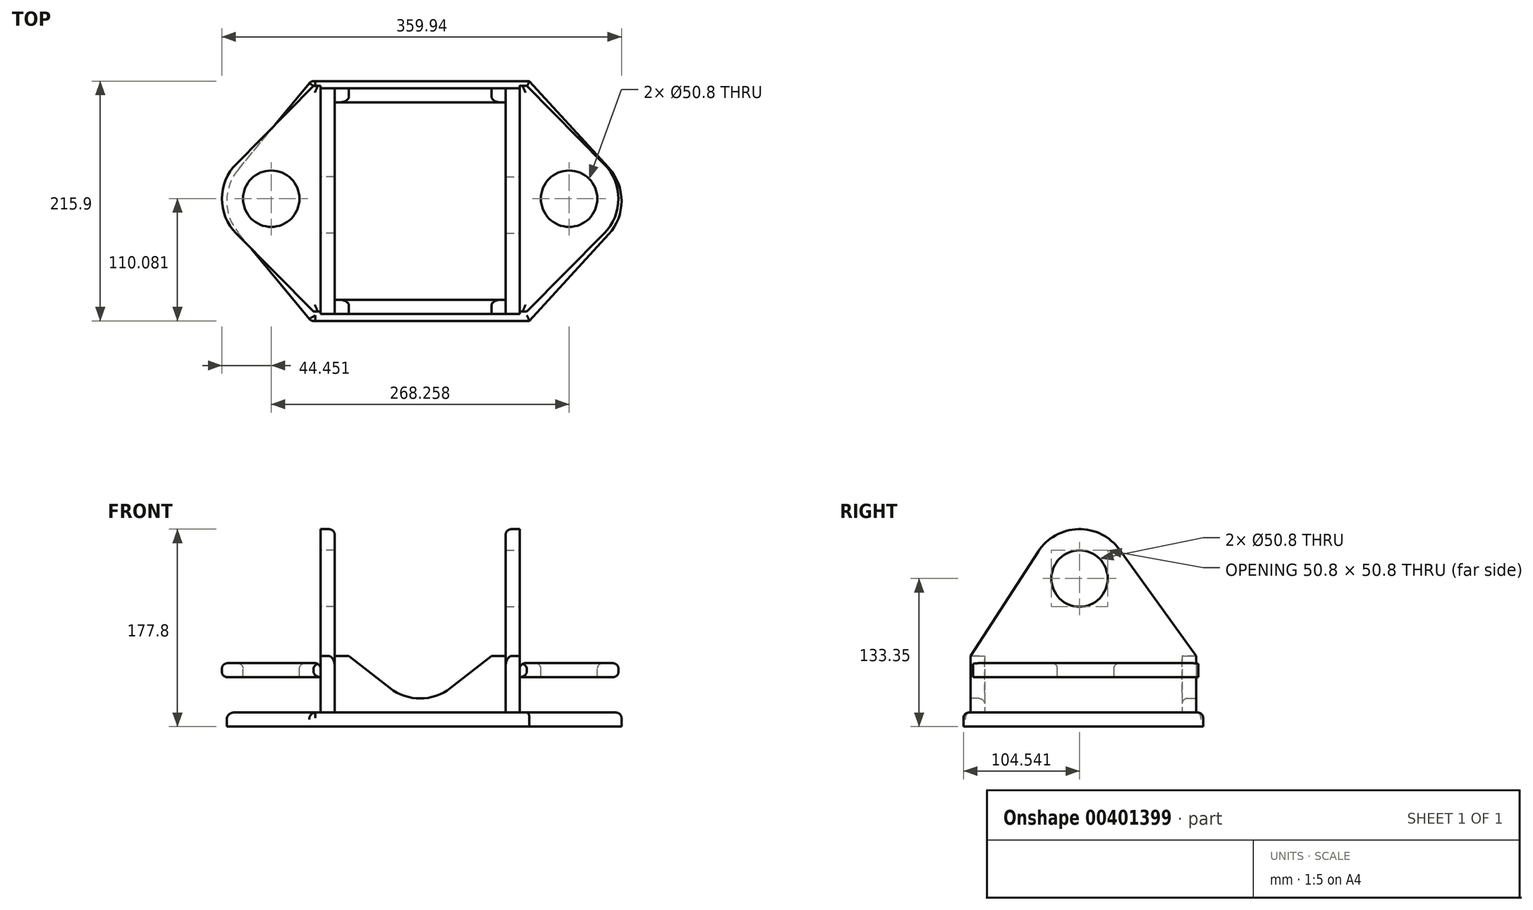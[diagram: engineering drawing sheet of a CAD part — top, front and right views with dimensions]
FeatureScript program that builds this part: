
annotation { "Feature Type Name" : "Feature", "Feature Type Description" : "" }
export const myFeature = defineFeature(function(context is Context, id is Id, definition is map)
    precondition{}
    {
        {
            var Q0;
            Q0=qCreatedBy(makeId("Top.planeOp"),FACE);
            var sketch = newSketch(context, id + "F0", { "sketchPlane" : qUnion([Q0])});
            skLineSegment(sketch, "E0.bottom", {"start": v(-98.42, 107.95) * mm, "end": v(98.43, 107.95) * mm});
            skLineSegment(sketch, "E0.top", {"start": v(-98.43, -107.95) * mm, "end": v(98.42, -107.95) * mm});
            skPoint(sketch, "E0.middle", {"position": v(0, 0) * mm});
            skArc(sketch, "E1", {"start": v(-164.1, 28.27) * mm, "mid": v(-174.24, 0) * mm, "end": v(-164.1, -28.27) * mm});
            skArc(sketch, "E2", {"start": v(169.7, -30) * mm, "mid": v(181.36, 0) * mm, "end": v(169.7, 30) * mm});
            skLineSegment(sketch, "E3", {"start": v(-98.43, -107.95) * mm, "end": v(-164.1, -28.27) * mm});
            skLineSegment(sketch, "E4", {"start": v(98.43, 107.95) * mm, "end": v(169.7, 30) * mm});
            skLineSegment(sketch, "E5", {"start": v(98.42, -107.95) * mm, "end": v(169.7, -30) * mm});
            skLineSegment(sketch, "E6", {"start": v(-98.43, 107.95) * mm, "end": v(-164.1, 28.27) * mm});
            skLineSegment(sketch, "E7", {"start": v(-174.24, 0) * mm, "end": v(181.36, 0) * mm, "construction": true});
            skSolve(sketch);
        }
        {
            var Q0;
            Q0 = qSketchRegion(id + "F0", true);
            extrude(context, id + "F1", {"entities" : qUnion([Q0]), "oppositeDirection" : true, "depth" : 12.7 * mm});
        }
        {
            var Q0;
            Q0=makeQuery(id+"F1.opExtrude","CAP_EDGE",EDGE,{"disambiguationData":[OSD([sQuery(id+"F0.wireOp",EDGE,"E6")])],"isStart":true});
            fillet(context, id + "F2", {"entities" : qUnion([Q0]), "radius" : 6.35 * mm, "tangentPropagation" : true, "allowEdgeOverflow" : false});
        }
        {
            var Q0;
            Q0=makeQuery(id+"F1.opExtrude","CAP_EDGE",EDGE,{"disambiguationData":[OSD([sQuery(id+"F0.wireOp",EDGE,"E0.bottom")])],"isStart":true});
            var Q1;
            Q1=makeQuery(id+"F1.opExtrude","CAP_EDGE",EDGE,{"disambiguationData":[OSD([sQuery(id+"F0.wireOp",EDGE,"E0.top")])],"isStart":true});
            var Q2;
            Q2=makeQuery(id+"F1.opExtrude","CAP_EDGE",EDGE,{"disambiguationData":[OSD([sQuery(id+"F0.wireOp",EDGE,"E5")])],"isStart":true});
            fillet(context, id + "F3", {"entities" : qUnion([Q0, Q1, Q2]), "radius" : 5.08 * mm, "tangentPropagation" : true, "allowEdgeOverflow" : false});
        }
        {
            var Q0;
            Q0=makeQuery(id+"F1.opExtrude","CAP_FACE",FACE,{"disambiguationData":[OSD([sQuery(id+"F0.wireOp",EDGE,"E0.bottom"),sQuery(id+"F0.wireOp",EDGE,"E0.top"),sQuery(id+"F0.wireOp",EDGE,"E1"),sQuery(id+"F0.wireOp",EDGE,"E2"),sQuery(id+"F0.wireOp",EDGE,"E3"),sQuery(id+"F0.wireOp",EDGE,"E4"),sQuery(id+"F0.wireOp",EDGE,"E5"),sQuery(id+"F0.wireOp",EDGE,"E6")])],"isStart":true});
            var sketch = newSketch(context, id + "F4", { "sketchPlane" : qUnion([Q0])});
            skLineSegment(sketch, "E8.bottom", {"start": v(-89.68, 101.6) * mm, "end": v(-76.98, 101.6) * mm});
            skLineSegment(sketch, "E8.top", {"start": v(-89.68, -101.6) * mm, "end": v(-76.98, -101.6) * mm});
            skLineSegment(sketch, "E8.left", {"start": v(-89.68, 101.6) * mm, "end": v(-89.68, -101.6) * mm});
            skLineSegment(sketch, "E8.right", {"start": v(-76.98, 101.6) * mm, "end": v(-76.98, -101.6) * mm});
            skSolve(sketch);
        }
        {
            var Q0;
            Q0 = qSketchRegion(id + "F4", true);
            extrude(context, id + "F5", {"entities" : qUnion([Q0]), "depth" : 165.1 * mm});
        }
        {
            var Q0;
            Q0=makeQuery(id+"F5.opExtrude","SWEPT_FACE",FACE,{"disambiguationData":[OSD([sQuery(id+"F4.wireOp",EDGE,"E8.left")])]});
            var sketch = newSketch(context, id + "F6", { "sketchPlane" : qUnion([Q0])});
            skLineSegment(sketch, "E9", {"start": v(-101.6, 50.8) * mm, "end": v(101.6, 50.8) * mm, "construction": true});
            skCircle(sketch, "E10", {"center": v(3.4, 120.65) * mm, "radius": 25.4 * mm});
            skArc(sketch, "E11", {"start": v(40.72, 144.81) * mm, "mid": v(4.5, 165.09) * mm, "end": v(-32.67, 146.6) * mm});
            skLineSegment(sketch, "E12", {"start": v(-101.6, 50.8) * mm, "end": v(-32.67, 146.6) * mm});
            skLineSegment(sketch, "E13", {"start": v(101.6, 50.8) * mm, "end": v(40.72, 144.81) * mm});
            skSolve(sketch);
        }
        {
            var Q0;
            Q0 = qSketchRegion(id + "F6", true);
            var Q1;
            {var subQ0=sQuery(id+"F6.wireOp",EDGE,"E12");Q1=makeQuery(id+"F6.imprint","IMPRINT",FACE,{"disambiguationData":[TD([[makeQuery(id+"F6.imprint","IMPRINT",EDGE,{"derivedFrom":subQ0}),1.0]])]});}
            var Q2;
            {var subQ0=sQuery(id+"F6.wireOp",EDGE,"E13");Q2=makeQuery(id+"F6.imprint","IMPRINT",FACE,{"disambiguationData":[TD([[makeQuery(id+"F6.imprint","IMPRINT",EDGE,{"derivedFrom":subQ0}),-1.0]])]});}
            extrude(context, id + "F7", {"entities" : qUnion([Q0, Q1, Q2]), "operationType" : NewBodyOperationType.REMOVE, "oppositeDirection" : true, "depth" : 25.4 * mm});
        }
        {
            var Q0;
            Q0=makeQuery(id+"F5.opExtrude","SWEPT_BODY",BODY,{"disambiguationData":[OSD([sQuery(id+"F4.wireOp",EDGE,"E8.bottom"),sQuery(id+"F4.wireOp",EDGE,"E8.top"),sQuery(id+"F4.wireOp",EDGE,"E8.left"),sQuery(id+"F4.wireOp",EDGE,"E8.right")])]});
            var Q1;
            Q1=qCreatedBy(makeId("Right.planeOp"),FACE);
            mirror(context, id + "F8", {"entities" : qUnion([Q0]), "mirrorPlane" : qUnion([Q1])});
        }
        {
            var Q0;
            Q0=makeQuery(id+"F1.opExtrude","CAP_FACE",FACE,{"disambiguationData":[OSD([sQuery(id+"F0.wireOp",EDGE,"E0.bottom"),sQuery(id+"F0.wireOp",EDGE,"E0.top"),sQuery(id+"F0.wireOp",EDGE,"E1"),sQuery(id+"F0.wireOp",EDGE,"E2"),sQuery(id+"F0.wireOp",EDGE,"E3"),sQuery(id+"F0.wireOp",EDGE,"E4"),sQuery(id+"F0.wireOp",EDGE,"E5"),sQuery(id+"F0.wireOp",EDGE,"E6")])],"isStart":true});
            var sketch = newSketch(context, id + "F9", { "sketchPlane" : qUnion([Q0])});
            skLineSegment(sketch, "E14.0", {"start": v(76.98, 101.6) * mm, "end": v(76.98, -101.6) * mm});
            skLineSegment(sketch, "E15.0", {"start": v(-76.98, 101.6) * mm, "end": v(-76.98, -101.6) * mm});
            skLineSegment(sketch, "E16.bottom", {"start": v(76.98, 101.6) * mm, "end": v(-76.98, 101.6) * mm});
            skLineSegment(sketch, "E16.top", {"start": v(76.98, 88.9) * mm, "end": v(-76.98, 88.9) * mm});
            skLineSegment(sketch, "E16.left", {"start": v(76.98, 101.6) * mm, "end": v(76.98, 88.9) * mm});
            skLineSegment(sketch, "E16.right", {"start": v(-76.98, 101.6) * mm, "end": v(-76.98, 88.9) * mm});
            skSolve(sketch);
        }
        {
            var Q0;
            Q0 = qSketchRegion(id + "F9", true);
            extrude(context, id + "F10", {"entities" : qUnion([Q0]), "depth" : 50.8 * mm});
        }
        {
            var Q0;
            Q0=makeQuery(id+"F10.opExtrude","SWEPT_FACE",FACE,{"disambiguationData":[OSD([sQuery(id+"F9.wireOp",EDGE,"E16.bottom")])]});
            var sketch = newSketch(context, id + "F11", { "sketchPlane" : qUnion([Q0])});
            skArc(sketch, "E17", {"start": v(-27.27, 22.05) * mm, "mid": v(0, 12.7) * mm, "end": v(27.27, 22.05) * mm});
            skPoint(sketch, "E17.centerSnap0", {"position": v(0, 50.8) * mm});
            skLineSegment(sketch, "E18", {"start": v(-64.28, 50.8) * mm, "end": v(-27.27, 22.05) * mm});
            skLineSegment(sketch, "E19", {"start": v(64.28, 50.8) * mm, "end": v(27.27, 22.05) * mm});
            skSolve(sketch);
        }
        {
            var Q0;
            Q0=makeQuery(id+"F11.imprint","IMPRINT",FACE,{"disambiguationData":[TD([[makeQuery(id+"F11.imprint","IMPRINT",EDGE,{"derivedFrom":sQuery(id+"F11.wireOp",EDGE,"E17")}),1.0]])]});
            var Q1;
            Q1=sQuery(id+"F11.wireOp",EDGE,"E18");
            var Q2;
            Q2=sQuery(id+"F11.wireOp",EDGE,"E17");
            var Q3;
            Q3=sQuery(id+"F11.wireOp",EDGE,"E19");
            extrude(context, id + "F12", {"entities" : qUnion([Q0]), "operationType" : NewBodyOperationType.REMOVE, "surfaceEntities" : qUnion([Q1, Q2, Q3]), "oppositeDirection" : true, "depth" : 25.4 * mm});
        }
        {
            var Q0;
            Q0=makeQuery(id+"F10.opExtrude","SWEPT_BODY",BODY,{"disambiguationData":[OSD([sQuery(id+"F9.wireOp",EDGE,"E16.bottom"),sQuery(id+"F9.wireOp",EDGE,"E16.top"),sQuery(id+"F9.wireOp",EDGE,"E16.left"),sQuery(id+"F9.wireOp",EDGE,"E16.right")])]});
            var Q1;
            Q1=qCreatedBy(makeId("Front.planeOp"),FACE);
            mirror(context, id + "F13", {"entities" : qUnion([Q0]), "mirrorPlane" : qUnion([Q1])});
        }
        {
            var Q0;
            Q0=makeQuery(id+"F7.boolean.opBoolean","COPY",EDGE,{"derivedFrom":makeQuery(id+"F7.opExtrude","CAP_EDGE",EDGE,{"disambiguationData":[OSD([sQuery(id+"F6.wireOp",EDGE,"E12")])],"isStart":true})});
            var Q1;
            {var subQ0=sQuery(id+"F6.wireOp",EDGE,"E11");Q1=makeQuery(id+"F7.boolean.opBoolean","TWEAK_EDGE",EDGE,{"derivedFrom":[makeQuery(id+"F7.opExtrude","CAP_EDGE",EDGE,{"disambiguationData":[OSD([subQ0]),TDD([makeQuery(id+"F6.imprint","IMPRINT",EDGE,{"disambiguationData":[TD([[makeQuery(id+"F6.imprint","INTERSECT",VERTEX,{"derivedFrom":[subQ0,sQuery(id+"F6.wireOp",EDGE,"E13")]}),-1.0]])],"derivedFrom":subQ0})])],"isStart":true}),makeQuery(id+"F7.opExtrude","CAP_EDGE",EDGE,{"disambiguationData":[OSD([subQ0]),TDD([makeQuery(id+"F6.imprint","IMPRINT",EDGE,{"disambiguationData":[TD([[makeQuery(id+"F6.imprint","INTERSECT",VERTEX,{"derivedFrom":[subQ0,sQuery(id+"F6.wireOp",EDGE,"E12")]}),1.0]])],"derivedFrom":subQ0})])],"isStart":true})]});}
            var Q2;
            Q2=makeQuery(id+"F7.boolean.opBoolean","COPY",EDGE,{"derivedFrom":makeQuery(id+"F7.opExtrude","CAP_EDGE",EDGE,{"disambiguationData":[OSD([sQuery(id+"F6.wireOp",EDGE,"E13")])],"isStart":true})});
            var Q3;
            Q3=makeQuery(id+"F8.opPattern","COPY",EDGE,{"derivedFrom":makeQuery(id+"F7.boolean.opBoolean","INTERSECT",EDGE,{"derivedFrom":[makeQuery(id+"F5.opExtrude","SWEPT_FACE",FACE,{"disambiguationData":[OSD([sQuery(id+"F4.wireOp",EDGE,"E8.right")])]}),makeQuery(id+"F7.opExtrude","SWEPT_FACE",FACE,{"disambiguationData":[OSD([sQuery(id+"F6.wireOp",EDGE,"E12")])]})]}),"instanceName":"1"});
            var Q4;
            Q4=makeQuery(id+"F8.opPattern","COPY",EDGE,{"derivedFrom":makeQuery(id+"F7.boolean.opBoolean","COPY",EDGE,{"derivedFrom":makeQuery(id+"F7.opExtrude","CAP_EDGE",EDGE,{"disambiguationData":[OSD([sQuery(id+"F6.wireOp",EDGE,"E12")])],"isStart":true})}),"instanceName":"1"});
            var Q5;
            Q5=makeQuery(id+"F7.boolean.opBoolean","INTERSECT",EDGE,{"derivedFrom":[makeQuery(id+"F5.opExtrude","SWEPT_FACE",FACE,{"disambiguationData":[OSD([sQuery(id+"F4.wireOp",EDGE,"E8.right")])]}),makeQuery(id+"F7.opExtrude","SWEPT_FACE",FACE,{"disambiguationData":[OSD([sQuery(id+"F6.wireOp",EDGE,"E12")])]})]});
            fillet(context, id + "F14", {"entities" : qUnion([Q0, Q1, Q2, Q3, Q4, Q5]), "radius" : 5.08 * mm, "tangentPropagation" : true, "allowEdgeOverflow" : false});
        }
        {
            var Q0;
            Q0=makeQuery(id+"F13.opPattern","COPY",EDGE,{"derivedFrom":makeQuery(id+"F12.boolean.opBoolean","COPY",EDGE,{"derivedFrom":makeQuery(id+"F12.opExtrude","CAP_EDGE",EDGE,{"disambiguationData":[OSD([sQuery(id+"F11.wireOp",EDGE,"E18")])],"isStart":true})}),"instanceName":"1"});
            var Q1;
            Q1=makeQuery(id+"F12.boolean.opBoolean","INTERSECT",EDGE,{"derivedFrom":[makeQuery(id+"F10.opExtrude","SWEPT_FACE",FACE,{"disambiguationData":[OSD([sQuery(id+"F9.wireOp",EDGE,"E16.top")])]}),makeQuery(id+"F12.opExtrude","SWEPT_FACE",FACE,{"disambiguationData":[OSD([sQuery(id+"F11.wireOp",EDGE,"E18")])]})]});
            var Q2;
            Q2=makeQuery(id+"F12.boolean.opBoolean","COPY",EDGE,{"derivedFrom":makeQuery(id+"F12.opExtrude","CAP_EDGE",EDGE,{"disambiguationData":[OSD([sQuery(id+"F11.wireOp",EDGE,"E19")])],"isStart":true})});
            var Q3;
            Q3=makeQuery(id+"F13.opPattern","COPY",EDGE,{"derivedFrom":makeQuery(id+"F12.boolean.opBoolean","INTERSECT",EDGE,{"derivedFrom":[makeQuery(id+"F10.opExtrude","SWEPT_FACE",FACE,{"disambiguationData":[OSD([sQuery(id+"F9.wireOp",EDGE,"E16.top")])]}),makeQuery(id+"F12.opExtrude","SWEPT_FACE",FACE,{"disambiguationData":[OSD([sQuery(id+"F11.wireOp",EDGE,"E19")])]})]}),"instanceName":"1"});
            fillet(context, id + "F15", {"entities" : qUnion([Q0, Q1, Q2, Q3]), "radius" : 5.08 * mm, "tangentPropagation" : true, "allowEdgeOverflow" : false});
        }
        {
            var Q0;
            Q0=makeQuery(id+"F8.opPattern","COPY",FACE,{"derivedFrom":makeQuery(id+"F5.opExtrude","SWEPT_FACE",FACE,{"disambiguationData":[OSD([sQuery(id+"F4.wireOp",EDGE,"E8.left")])]}),"instanceName":"1"});
            var sketch = newSketch(context, id + "F16", { "sketchPlane" : qUnion([Q0])});
            skLineSegment(sketch, "E20.bottom", {"start": v(-99.47, 44.45) * mm, "end": v(103.73, 44.45) * mm});
            skLineSegment(sketch, "E20.top", {"start": v(-99.47, 31.75) * mm, "end": v(103.73, 31.75) * mm});
            skLineSegment(sketch, "E20.left", {"start": v(-99.47, 44.45) * mm, "end": v(-99.47, 31.75) * mm});
            skLineSegment(sketch, "E20.right", {"start": v(103.73, 44.45) * mm, "end": v(103.73, 31.75) * mm});
            skSolve(sketch);
        }
        {
            var Q0;
            Q0 = qSketchRegion(id + "F16", true);
            extrude(context, id + "F17", {"entities" : qUnion([Q0]), "depth" : 88.9 * mm});
        }
        {
            var Q0;
            Q0=makeQuery(id+"F17.opExtrude","SWEPT_FACE",FACE,{"disambiguationData":[OSD([sQuery(id+"F16.wireOp",EDGE,"E20.bottom")])]});
            var sketch = newSketch(context, id + "F18", { "sketchPlane" : qUnion([Q0])});
            skPoint(sketch, "E21.centerSnap0", {"position": v(178.58, 2.13) * mm});
            skCircle(sketch, "E22", {"center": v(134.13, 2.13) * mm, "radius": 25.4 * mm});
            skLineSegment(sketch, "E23", {"start": v(96.03, 103.73) * mm, "end": v(96.03, -99.47) * mm, "construction": true});
            skLineSegment(sketch, "E24", {"start": v(96.03, 103.73) * mm, "end": v(165.7, 33.42) * mm});
            skLineSegment(sketch, "E25", {"start": v(96.03, -99.47) * mm, "end": v(165.7, -29.16) * mm});
            skArc(sketch, "E26.trimOffspring", {"start": v(165.7, -29.16) * mm, "mid": v(178.58, 2.13) * mm, "end": v(165.7, 33.42) * mm});
            skSolve(sketch);
        }
        {
            var Q0;
            Q0 = qSketchRegion(id + "F18", true);
            var Q1;
            {var subQ0=sQuery(id+"F18.wireOp",EDGE,"E24");Q1=makeQuery(id+"F18.imprint","IMPRINT",FACE,{"disambiguationData":[TD([[makeQuery(id+"F18.imprint","IMPRINT",EDGE,{"derivedFrom":subQ0}),1.0]])]});}
            var Q2;
            {var subQ0=sQuery(id+"F18.wireOp",EDGE,"E25");Q2=makeQuery(id+"F18.imprint","IMPRINT",FACE,{"disambiguationData":[TD([[makeQuery(id+"F18.imprint","IMPRINT",EDGE,{"derivedFrom":subQ0}),-1.0]])]});}
            extrude(context, id + "F19", {"entities" : qUnion([Q0, Q1, Q2]), "operationType" : NewBodyOperationType.REMOVE, "oppositeDirection" : true, "depth" : 25.4 * mm});
        }
        {
            var Q0;
            Q0=makeQuery(id+"F17.opExtrude","SWEPT_FACE",FACE,{"disambiguationData":[OSD([sQuery(id+"F16.wireOp",EDGE,"E20.bottom")])]});
            var Q1;
            Q1=makeQuery(id+"F19.boolean.opBoolean","COPY",EDGE,{"derivedFrom":makeQuery(id+"F19.opExtrude","CAP_EDGE",EDGE,{"disambiguationData":[OSD([sQuery(id+"F18.wireOp",EDGE,"E25")])],"isStart":true})});
            var Q2;
            Q2=makeQuery(id+"F19.boolean.opBoolean","INTERSECT",EDGE,{"derivedFrom":[makeQuery(id+"F17.opExtrude","SWEPT_FACE",FACE,{"disambiguationData":[OSD([sQuery(id+"F16.wireOp",EDGE,"E20.top")])]}),makeQuery(id+"F19.opExtrude","SWEPT_FACE",FACE,{"disambiguationData":[OSD([sQuery(id+"F18.wireOp",EDGE,"E25")])]})]});
            fillet(context, id + "F20", {"entities" : qUnion([Q0, Q1, Q2]), "radius" : 5.08 * mm, "tangentPropagation" : true, "allowEdgeOverflow" : false});
        }
        {
            var Q0;
            Q0=makeQuery(id+"F17.opExtrude","SWEPT_BODY",BODY,{"disambiguationData":[OSD([sQuery(id+"F16.wireOp",EDGE,"E20.bottom"),sQuery(id+"F16.wireOp",EDGE,"E20.top"),sQuery(id+"F16.wireOp",EDGE,"E20.left"),sQuery(id+"F16.wireOp",EDGE,"E20.right")])]});
            var Q1;
            Q1=qCreatedBy(makeId("Right.planeOp"),FACE);
            mirror(context, id + "F21", {"entities" : qUnion([Q0]), "mirrorPlane" : qUnion([Q1])});
        }
    });
